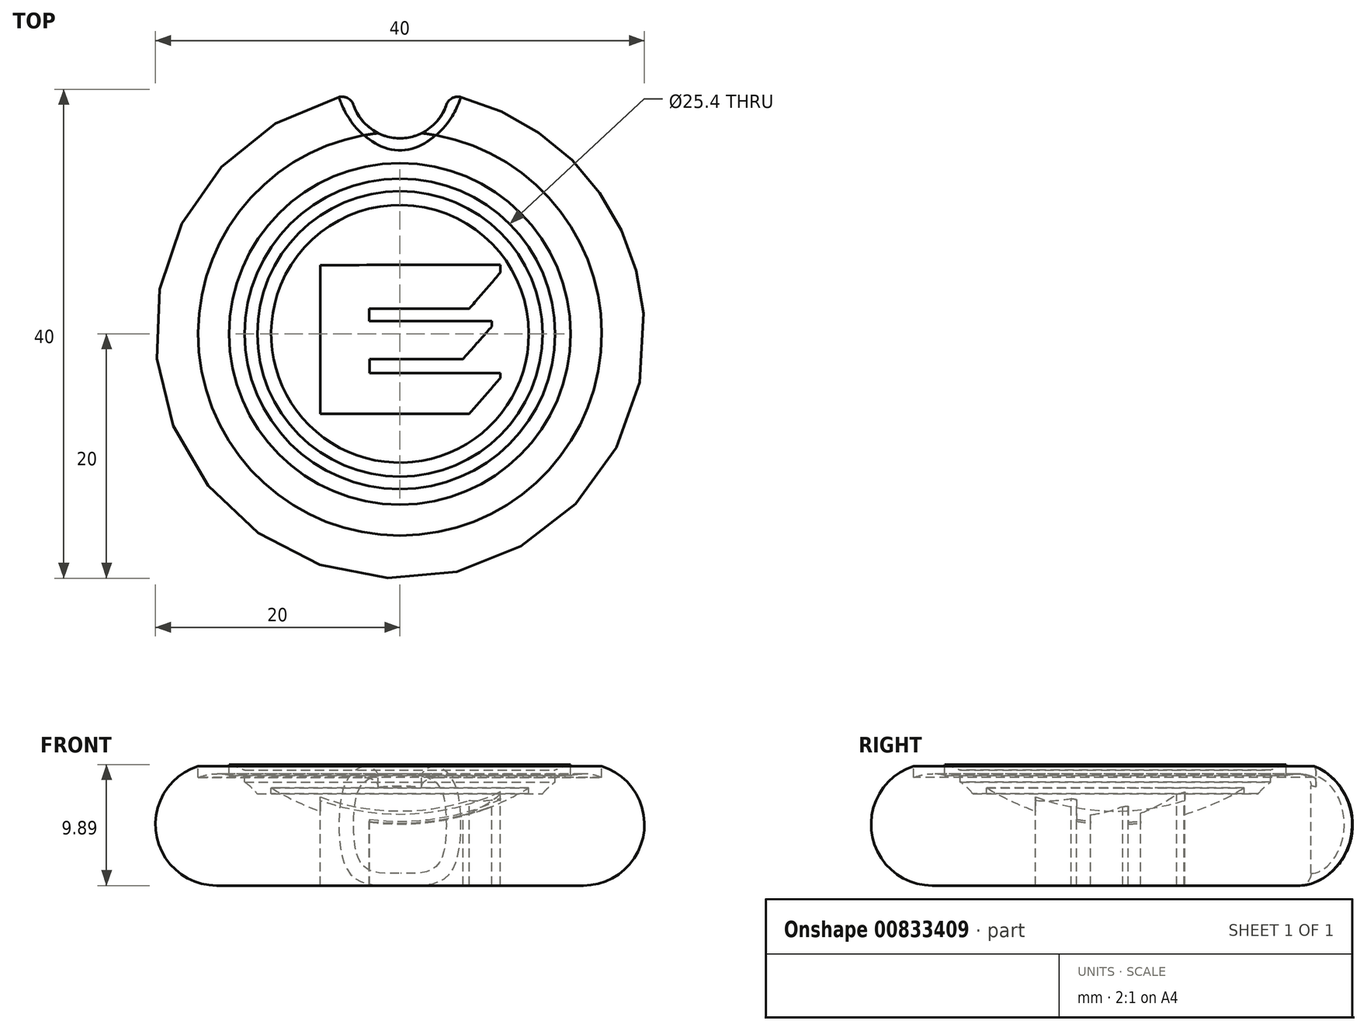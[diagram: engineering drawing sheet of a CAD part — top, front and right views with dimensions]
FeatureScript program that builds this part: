
annotation { "Feature Type Name" : "Feature", "Feature Type Description" : "" }
export const myFeature = defineFeature(function(context is Context, id is Id, definition is map)
    precondition{}
    {
        {
            var Q0;
            Q0=qCreatedBy(makeId("Front.planeOp"),FACE);
            var sketch = newSketch(context, id + "F0", { "sketchPlane" : qUnion([Q0])});
            skArc(sketch, "E0", {"start": v(-12, 9) * mm, "mid": v(-6.32, 6.03) * mm, "end": v(0, 5) * mm});
            skArc(sketch, "E1", {"start": v(-12, 9) * mm, "mid": v(-19.74, 6.58) * mm, "end": v(-15, 0) * mm});
            skLineSegment(sketch, "E2", {"start": v(0, 5) * mm, "end": v(0, 0) * mm});
            skLineSegment(sketch, "E3", {"start": v(0, 0) * mm, "end": v(-15, 0) * mm});
            skSolve(sketch);
        }
        {
            var Q0;
            Q0=makeQuery(id+"F0.imprint","IMPRINT",FACE,{"disambiguationData":[TD([[makeQuery(id+"F0.imprint","IMPRINT",EDGE,{"derivedFrom":sQuery(id+"F0.wireOp",EDGE,"E0")}),-1.0]])]});
            var Q1;
            Q1=sQuery(id+"F0.wireOp",EDGE,"E2");
            revolve(context, id + "F1", {"surfaceOperationType" : NewSurfaceOperationType.NEW, "entities" : qUnion([Q0]), "axis" : qUnion([Q1]), "revolveType" : RevolveType.FULL});
        }
        {
            var Q0;
            Q0=qCreatedBy(makeId("Top.planeOp"),FACE);
            cPlane(context, id + "F2", {"entities" : qUnion([Q0]), "cplaneType" : CPlaneType.OFFSET, "offset" : 10 * mm, "width" : 152.4 * mm, "height" : 152.4 * mm});
        }
        {
            var Q0;
            Q0=qCreatedBy(id+"F2.planeOp",FACE);
            var sketch = newSketch(context, id + "F3", { "sketchPlane" : qUnion([Q0])});
            skLineSegment(sketch, "E4", {"start": v(-6.53, 5.62) * mm, "end": v(-6.53, -6.54) * mm});
            skLineSegment(sketch, "E5", {"start": v(-6.53, -6.54) * mm, "end": v(5.67, -6.54) * mm});
            skLineSegment(sketch, "E6", {"start": v(5.67, -6.54) * mm, "end": v(8.2, -3.64) * mm});
            skLineSegment(sketch, "E7", {"start": v(8.2, -3.64) * mm, "end": v(8.2, -3.2) * mm});
            skLineSegment(sketch, "E8", {"start": v(8.2, -3.2) * mm, "end": v(-2.49, -3.2) * mm});
            skLineSegment(sketch, "E9", {"start": v(-2.49, -3.2) * mm, "end": v(-2.49, -2.06) * mm});
            skLineSegment(sketch, "E10", {"start": v(-2.49, -2.06) * mm, "end": v(5.16, -2.06) * mm});
            skLineSegment(sketch, "E11", {"start": v(5.16, -2.06) * mm, "end": v(7.5, 0.59) * mm});
            skLineSegment(sketch, "E12", {"start": v(7.5, 0.59) * mm, "end": v(7.5, 1.03) * mm});
            skLineSegment(sketch, "E13", {"start": v(7.5, 1.03) * mm, "end": v(-2.52, 1.03) * mm});
            skLineSegment(sketch, "E14", {"start": v(-2.52, 1.03) * mm, "end": v(-2.52, 2.06) * mm});
            skLineSegment(sketch, "E15", {"start": v(-2.52, 2.06) * mm, "end": v(5.67, 2.06) * mm});
            skLineSegment(sketch, "E16", {"start": v(5.67, 2.06) * mm, "end": v(8.2, 5) * mm});
            skLineSegment(sketch, "E17", {"start": v(8.2, 5) * mm, "end": v(8.2, 5.66) * mm});
            skLineSegment(sketch, "E18", {"start": v(8.2, 5.66) * mm, "end": v(-6.53, 5.62) * mm});
            skCircle(sketch, "E19", {"center": v(0, 0) * mm, "radius": 10.54 * mm});
            skCircle(sketch, "E20", {"center": v(0, 0) * mm, "radius": 13.97 * mm});
            skCircle(sketch, "E21", {"center": v(0, 0) * mm, "radius": 12.7 * mm});
            skCircle(sketch, "E22", {"center": v(0, 0) * mm, "radius": 16.51 * mm});
            skSolve(sketch);
        }
        {
            var Q0;
            Q0=makeQuery(id+"F3.imprint","IMPRINT",FACE,{"disambiguationData":[TD([[makeQuery(id+"F3.imprint","IMPRINT",EDGE,{"derivedFrom":sQuery(id+"F3.wireOp",EDGE,"E4")}),1.0]])]});
            extrude(context, id + "F4", {"entities" : qUnion([Q0]), "operationType" : NewBodyOperationType.REMOVE, "oppositeDirection" : true, "depth" : 15 * mm, "offsetDistance" : 25.4 * mm});
        }
        {
            var Q0;
            Q0=makeQuery(id+"F3.imprint","IMPRINT",FACE,{"disambiguationData":[TD([[makeQuery(id+"F3.imprint","IMPRINT",EDGE,{"derivedFrom":sQuery(id+"F3.wireOp",EDGE,"E19")}),-1.0]])]});
            extrude(context, id + "F5", {"entities" : qUnion([Q0]), "operationType" : NewBodyOperationType.REMOVE, "oppositeDirection" : true, "depth" : 2.5 * mm, "offsetDistance" : 25.4 * mm});
        }
        {
            var Q0;
            Q0=makeQuery(id+"F3.imprint","IMPRINT",FACE,{"disambiguationData":[TD([[makeQuery(id+"F3.imprint","IMPRINT",EDGE,{"derivedFrom":sQuery(id+"F3.wireOp",EDGE,"E20")}),-1.0]])]});
            var Q1;
            Q1=sQuery(id+"F3.wireOp",EDGE,"E22");
            var Q2;
            Q2=sQuery(id+"F3.wireOp",EDGE,"E21");
            extrude(context, id + "F6", {"entities" : qUnion([Q0]), "operationType" : NewBodyOperationType.REMOVE, "surfaceEntities" : qUnion([Q1, Q2]), "oppositeDirection" : true, "depth" : 2.5 * mm, "offsetDistance" : 25.4 * mm});
        }
        {
            var Q0;
            Q0=qCreatedBy(makeId("Front.planeOp"),FACE);
            var sketch = newSketch(context, id + "F7", { "sketchPlane" : qUnion([Q0])});
            skCircle(sketch, "E23", {"center": v(-14.97, 5) * mm, "radius": 4.14 * mm});
            skSolve(sketch);
        }
        {
            var Q0;
            Q0 = qSketchRegion(id + "F7", true);
            var Q1;
            Q1=sQuery(id+"F0.wireOp",EDGE,"E2");
            revolve(context, id + "F8", {"operationType" : NewBodyOperationType.ADD, "surfaceOperationType" : NewSurfaceOperationType.NEW, "entities" : qUnion([Q0]), "axis" : qUnion([Q1]), "revolveType" : RevolveType.FULL});
        }
        {
            var Q0;
            Q0=qCreatedBy(id+"F2.planeOp",FACE);
            var sketch = newSketch(context, id + "F9", { "sketchPlane" : qUnion([Q0])});
            skCircle(sketch, "E24", {"center": v(0, 20) * mm, "radius": 4 * mm});
            skSolve(sketch);
        }
        {
            var Q0;
            Q0 = qSketchRegion(id + "F9", true);
            extrude(context, id + "F10", {"entities" : qUnion([Q0]), "operationType" : NewBodyOperationType.REMOVE, "oppositeDirection" : true, "depth" : 25.4 * mm, "offsetDistance" : 25.4 * mm});
        }
        {
            var Q0;
            Q0=makeQuery(id+"F10.boolean.opBoolean","INTERSECT",EDGE,{"derivedFrom":[makeQuery(id+"F6.boolean.opBoolean","SPLIT",FACE,{"disambiguationData":[TD([makeQuery(id+"F1.opRevolve","SWEPT_FACE",FACE,{"disambiguationData":[OSD([sQuery(id+"F0.wireOp",EDGE,"E3")])]})])],"derivedFrom":makeQuery(id+"F1.opRevolve","SWEPT_FACE",FACE,{"disambiguationData":[OSD([sQuery(id+"F0.wireOp",EDGE,"E1")])]})}),makeQuery(id+"F10.opExtrude","SWEPT_FACE",FACE,{"disambiguationData":[OSD([sQuery(id+"F9.wireOp",EDGE,"E24")])]})]});
            fillet(context, id + "F11", {"entities" : qUnion([Q0]), "radius" : 1 * mm, "tangentPropagation" : true, "allowEdgeOverflow" : false});
        }
        {
            var Q0;
            Q0=makeQuery(id+"FEgyx91S3JllC8I_1.7.F10.boolean.opBoolean","INTERSECT",EDGE,{"derivedFrom":[makeQuery(id+"F8.boolean.opBoolean","SPLIT",FACE,{"disambiguationData":[TD([makeQuery(id+"F6.boolean.opBoolean","COPY",FACE,{"derivedFrom":makeQuery(id+"F6.opExtrude","SWEPT_FACE",FACE,{"disambiguationData":[OSD([sQuery(id+"F3.wireOp",EDGE,"E20")])]})})])],"derivedFrom":makeQuery(id+"F8.opRevolve","SWEPT_FACE",FACE,{"disambiguationData":[OSD([sQuery(id+"F7.wireOp",EDGE,"E23")])]})}),makeQuery(id+"FEgyx91S3JllC8I_1.7.F10.opExtrude","SWEPT_FACE",FACE,{"disambiguationData":[OSD([sQuery(id+"F9.wireOp",EDGE,"E24")])]})]});
            var Q1;
            Q1=makeQuery(id+"FEgyx91S3JllC8I_1.6.F10.boolean.opBoolean","INTERSECT",EDGE,{"derivedFrom":[makeQuery(id+"F8.boolean.opBoolean","SPLIT",FACE,{"disambiguationData":[TD([makeQuery(id+"F6.boolean.opBoolean","COPY",FACE,{"derivedFrom":makeQuery(id+"F6.opExtrude","SWEPT_FACE",FACE,{"disambiguationData":[OSD([sQuery(id+"F3.wireOp",EDGE,"E20")])]})})])],"derivedFrom":makeQuery(id+"F8.opRevolve","SWEPT_FACE",FACE,{"disambiguationData":[OSD([sQuery(id+"F7.wireOp",EDGE,"E23")])]})}),makeQuery(id+"FEgyx91S3JllC8I_1.6.F10.opExtrude","SWEPT_FACE",FACE,{"disambiguationData":[OSD([sQuery(id+"F9.wireOp",EDGE,"E24")])]})]});
            var Q2;
            Q2=makeQuery(id+"FEgyx91S3JllC8I_1.5.F10.boolean.opBoolean","INTERSECT",EDGE,{"derivedFrom":[makeQuery(id+"F8.boolean.opBoolean","SPLIT",FACE,{"disambiguationData":[TD([makeQuery(id+"F6.boolean.opBoolean","COPY",FACE,{"derivedFrom":makeQuery(id+"F6.opExtrude","SWEPT_FACE",FACE,{"disambiguationData":[OSD([sQuery(id+"F3.wireOp",EDGE,"E20")])]})})])],"derivedFrom":makeQuery(id+"F8.opRevolve","SWEPT_FACE",FACE,{"disambiguationData":[OSD([sQuery(id+"F7.wireOp",EDGE,"E23")])]})}),makeQuery(id+"FEgyx91S3JllC8I_1.5.F10.opExtrude","SWEPT_FACE",FACE,{"disambiguationData":[OSD([sQuery(id+"F9.wireOp",EDGE,"E24")])]})]});
            var Q3;
            Q3=makeQuery(id+"FEgyx91S3JllC8I_1.4.F10.boolean.opBoolean","INTERSECT",EDGE,{"derivedFrom":[makeQuery(id+"F8.boolean.opBoolean","SPLIT",FACE,{"disambiguationData":[TD([makeQuery(id+"F6.boolean.opBoolean","COPY",FACE,{"derivedFrom":makeQuery(id+"F6.opExtrude","SWEPT_FACE",FACE,{"disambiguationData":[OSD([sQuery(id+"F3.wireOp",EDGE,"E20")])]})})])],"derivedFrom":makeQuery(id+"F8.opRevolve","SWEPT_FACE",FACE,{"disambiguationData":[OSD([sQuery(id+"F7.wireOp",EDGE,"E23")])]})}),makeQuery(id+"FEgyx91S3JllC8I_1.4.F10.opExtrude","SWEPT_FACE",FACE,{"disambiguationData":[OSD([sQuery(id+"F9.wireOp",EDGE,"E24")])]})]});
            var Q4;
            Q4=makeQuery(id+"FEgyx91S3JllC8I_1.3.F10.boolean.opBoolean","INTERSECT",EDGE,{"derivedFrom":[makeQuery(id+"F8.boolean.opBoolean","SPLIT",FACE,{"disambiguationData":[TD([makeQuery(id+"F6.boolean.opBoolean","COPY",FACE,{"derivedFrom":makeQuery(id+"F6.opExtrude","SWEPT_FACE",FACE,{"disambiguationData":[OSD([sQuery(id+"F3.wireOp",EDGE,"E20")])]})})])],"derivedFrom":makeQuery(id+"F8.opRevolve","SWEPT_FACE",FACE,{"disambiguationData":[OSD([sQuery(id+"F7.wireOp",EDGE,"E23")])]})}),makeQuery(id+"FEgyx91S3JllC8I_1.3.F10.opExtrude","SWEPT_FACE",FACE,{"disambiguationData":[OSD([sQuery(id+"F9.wireOp",EDGE,"E24")])]})]});
            var Q5;
            Q5=makeQuery(id+"F10.boolean.opBoolean","INTERSECT",EDGE,{"derivedFrom":[makeQuery(id+"F8.boolean.opBoolean","SPLIT",FACE,{"disambiguationData":[TD([makeQuery(id+"F6.boolean.opBoolean","COPY",FACE,{"derivedFrom":makeQuery(id+"F6.opExtrude","SWEPT_FACE",FACE,{"disambiguationData":[OSD([sQuery(id+"F3.wireOp",EDGE,"E20")])]})})])],"derivedFrom":makeQuery(id+"F8.opRevolve","SWEPT_FACE",FACE,{"disambiguationData":[OSD([sQuery(id+"F7.wireOp",EDGE,"E23")])]})}),makeQuery(id+"F10.opExtrude","SWEPT_FACE",FACE,{"disambiguationData":[OSD([sQuery(id+"F9.wireOp",EDGE,"E24")])]})]});
            var Q6;
            Q6=makeQuery(id+"FEgyx91S3JllC8I_1.2.F10.boolean.opBoolean","INTERSECT",EDGE,{"derivedFrom":[makeQuery(id+"F8.boolean.opBoolean","SPLIT",FACE,{"disambiguationData":[TD([makeQuery(id+"F6.boolean.opBoolean","COPY",FACE,{"derivedFrom":makeQuery(id+"F6.opExtrude","SWEPT_FACE",FACE,{"disambiguationData":[OSD([sQuery(id+"F3.wireOp",EDGE,"E20")])]})})])],"derivedFrom":makeQuery(id+"F8.opRevolve","SWEPT_FACE",FACE,{"disambiguationData":[OSD([sQuery(id+"F7.wireOp",EDGE,"E23")])]})}),makeQuery(id+"FEgyx91S3JllC8I_1.2.F10.opExtrude","SWEPT_FACE",FACE,{"disambiguationData":[OSD([sQuery(id+"F9.wireOp",EDGE,"E24")])]})]});
            var Q7;
            Q7=makeQuery(id+"FEgyx91S3JllC8I_1.1.F10.boolean.opBoolean","INTERSECT",EDGE,{"derivedFrom":[makeQuery(id+"F8.boolean.opBoolean","SPLIT",FACE,{"disambiguationData":[TD([makeQuery(id+"F6.boolean.opBoolean","COPY",FACE,{"derivedFrom":makeQuery(id+"F6.opExtrude","SWEPT_FACE",FACE,{"disambiguationData":[OSD([sQuery(id+"F3.wireOp",EDGE,"E20")])]})})])],"derivedFrom":makeQuery(id+"F8.opRevolve","SWEPT_FACE",FACE,{"disambiguationData":[OSD([sQuery(id+"F7.wireOp",EDGE,"E23")])]})}),makeQuery(id+"FEgyx91S3JllC8I_1.1.F10.opExtrude","SWEPT_FACE",FACE,{"disambiguationData":[OSD([sQuery(id+"F9.wireOp",EDGE,"E24")])]})]});
            fillet(context, id + "F12", {"entities" : qUnion([Q0, Q1, Q2, Q3, Q4, Q5, Q6, Q7]), "radius" : 1 * mm, "tangentPropagation" : true, "allowEdgeOverflow" : false});
        }
    });
